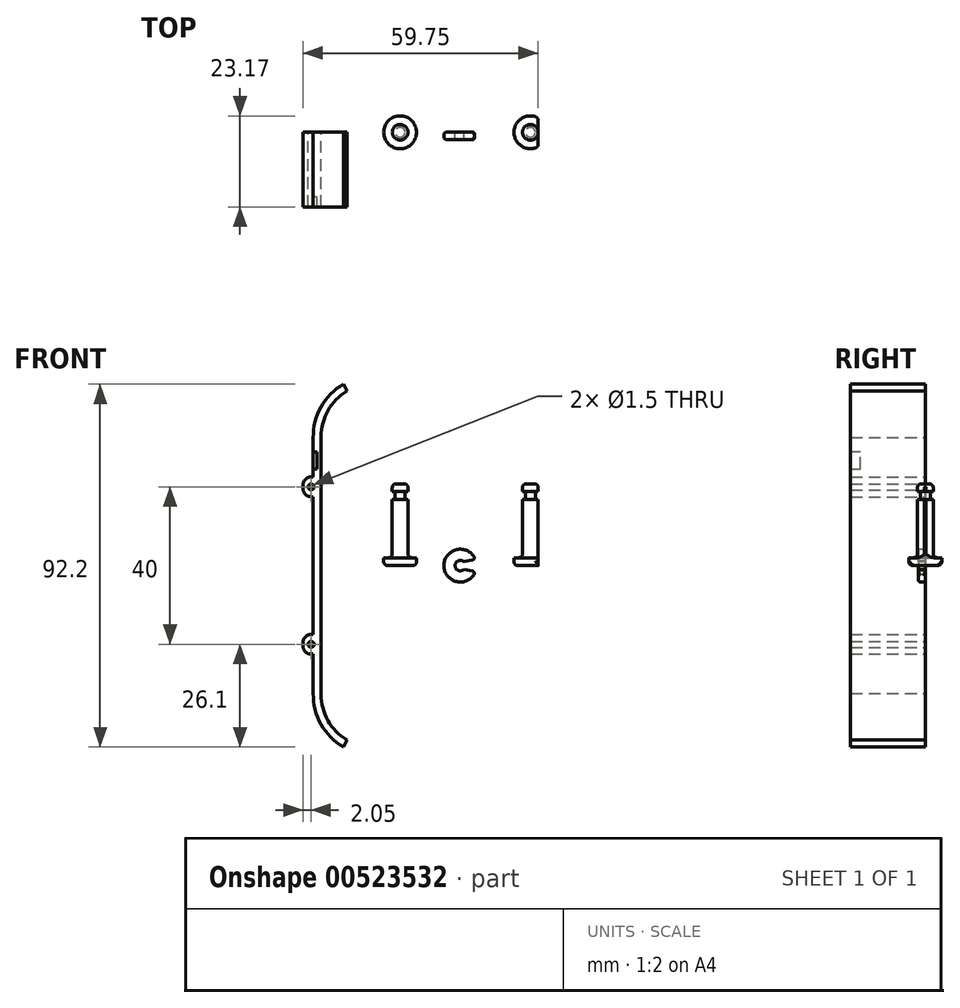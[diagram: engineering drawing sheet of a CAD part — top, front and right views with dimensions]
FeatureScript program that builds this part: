
annotation { "Feature Type Name" : "Feature", "Feature Type Description" : "" }
export const myFeature = defineFeature(function(context is Context, id is Id, definition is map)
    precondition{}
    {
        {
            var Q0;
            Q0=qCreatedBy(makeId("Front.planeOp"),FACE);
            var sketch = newSketch(context, id + "F0", { "sketchPlane" : qUnion([Q0])});
            skLineSegment(sketch, "E0", {"start": v(0, -32.75) * mm, "end": v(0, 32.75) * mm});
            skLineSegment(sketch, "E1", {"start": v(16.3, 46.1) * mm, "end": v(-10.09, 46.1) * mm, "construction": true});
            skLineSegment(sketch, "E2", {"start": v(9, 15.43) * mm, "end": v(9, 51.44) * mm, "construction": true});
            skArc(sketch, "E3.trimOffspring", {"start": v(6.55, 44.32) * mm, "mid": v(1.75, 39.4) * mm, "end": v(0, 32.75) * mm});
            skLineSegment(sketch, "E4", {"start": v(-2, -32.5) * mm, "end": v(-2, -22.5) * mm});
            skArc(sketch, "E5.trimOffspring", {"start": v(5.63, 46.1) * mm, "mid": v(-0.02, 40.33) * mm, "end": v(-2, 32.5) * mm});
            skLineSegment(sketch, "E6", {"start": v(-2, 17.5) * mm, "end": v(-4.6, 17.5) * mm});
            skLineSegment(sketch, "E7", {"start": v(-4.6, 17.5) * mm, "end": v(-4.6, 22.5) * mm});
            skLineSegment(sketch, "E8", {"start": v(-4.6, 22.5) * mm, "end": v(-2, 22.5) * mm});
            skCircle(sketch, "E9", {"center": v(-2.55, 20) * mm, "radius": 0.75 * mm});
            skLineSegment(sketch, "E10.trimOffspring", {"start": v(-2, 22.5) * mm, "end": v(-2, 32.5) * mm});
            skCircle(sketch, "E11.MirrorC", {"center": v(-2.55, -20) * mm, "radius": 0.75 * mm});
            skLineSegment(sketch, "E12.MirrorCS", {"start": v(-2, -17.5) * mm, "end": v(-4.6, -17.5) * mm});
            skLineSegment(sketch, "E13.MirrorCS", {"start": v(-4.6, -22.5) * mm, "end": v(-2, -22.5) * mm});
            skLineSegment(sketch, "E14.MirrorCS", {"start": v(-4.6, -17.5) * mm, "end": v(-4.6, -22.5) * mm});
            skLineSegment(sketch, "E15.trimOffspring", {"start": v(-2, -17.5) * mm, "end": v(-2, 17.5) * mm});
            skPoint(sketch, "E16", {"position": v(-0.02, 40.33) * mm});
            skPoint(sketch, "E17", {"position": v(1.75, 39.4) * mm});
            skLineSegment(sketch, "E18", {"start": v(5.63, 46.1) * mm, "end": v(6.55, 44.32) * mm});
            skArc(sketch, "E19.MirrorCS", {"start": v(6.55, -44.32) * mm, "mid": v(1.75, -39.4) * mm, "end": v(0, -32.75) * mm});
            skArc(sketch, "E20.MirrorCS", {"start": v(5.63, -46.1) * mm, "mid": v(-0.02, -40.33) * mm, "end": v(-2, -32.5) * mm});
            skLineSegment(sketch, "E21.MirrorCS", {"start": v(5.63, -46.1) * mm, "end": v(6.55, -44.32) * mm});
            skSolve(sketch);
        }
        {
            var Q0;
            Q0=makeQuery(id+"F0.imprint","IMPRINT",FACE,{"disambiguationData":[TD([[makeQuery(id+"F0.imprint","IMPRINT",EDGE,{"derivedFrom":sQuery(id+"F0.wireOp",EDGE,"E0")}),1.0]])]});
            extrude(context, id + "F1", {"entities" : qUnion([Q0]), "depth" : 19 * mm, "offsetDistance" : 25 * mm});
        }
        {
            var Q0;
            Q0=makeQuery(id+"F1.opExtrude","SWEPT_EDGE",EDGE,{"disambiguationData":[OSD([sQuery(id+"F0.wireOp",EDGE,"E7"),sQuery(id+"F0.wireOp",EDGE,"E8")])]});
            var Q1;
            Q1=makeQuery(id+"F1.opExtrude","SWEPT_EDGE",EDGE,{"disambiguationData":[OSD([sQuery(id+"F0.wireOp",EDGE,"E6"),sQuery(id+"F0.wireOp",EDGE,"E7")])]});
            var Q2;
            Q2=makeQuery(id+"F1.opExtrude","SWEPT_EDGE",EDGE,{"disambiguationData":[OSD([sQuery(id+"F0.wireOp",EDGE,"E12.MirrorCS"),sQuery(id+"F0.wireOp",EDGE,"E14.MirrorCS")])]});
            var Q3;
            Q3=makeQuery(id+"F1.opExtrude","SWEPT_EDGE",EDGE,{"disambiguationData":[OSD([sQuery(id+"F0.wireOp",EDGE,"E13.MirrorCS"),sQuery(id+"F0.wireOp",EDGE,"E14.MirrorCS")])]});
            fillet(context, id + "F2", {"entities" : qUnion([Q0, Q1, Q2, Q3]), "radius" : 2 * mm, "tangentPropagation" : true, "allowEdgeOverflow" : false});
        }
        {
            var Q0;
            Q0=makeQuery(id+"F1.opExtrude","SWEPT_FACE",FACE,{"disambiguationData":[OSD([sQuery(id+"F0.wireOp",EDGE,"E10.trimOffspring")])]});
            var sketch = newSketch(context, id + "F3", { "sketchPlane" : qUnion([Q0])});
            skLineSegment(sketch, "E22", {"start": v(19, 24.6) * mm, "end": v(16.5, 24.6) * mm});
            skLineSegment(sketch, "E23", {"start": v(16.5, 24.6) * mm, "end": v(16.5, 28.86) * mm});
            skLineSegment(sketch, "E24", {"start": v(16.5, 28.86) * mm, "end": v(19, 28.86) * mm});
            skLineSegment(sketch, "E25", {"start": v(19, 24.6) * mm, "end": v(19, 28.86) * mm});
            skSolve(sketch);
        }
        {
            var Q0;
            Q0=makeQuery(id+"F3.imprint","IMPRINT",FACE,{"disambiguationData":[TD([[makeQuery(id+"F3.imprint","IMPRINT",EDGE,{"derivedFrom":sQuery(id+"F3.wireOp",EDGE,"E22")}),-1.0]])]});
            extrude(context, id + "F4", {"entities" : qUnion([Q0]), "operationType" : NewBodyOperationType.REMOVE, "oppositeDirection" : true, "depth" : 1 * mm, "offsetDistance" : 25 * mm});
        }
        {
            var Q0;
            Q0=qCreatedBy(makeId("Front.planeOp"),FACE);
            var sketch = newSketch(context, id + "F5", { "sketchPlane" : qUnion([Q0])});
            skLineSegment(sketch, "E26", {"start": v(20.07, 0) * mm, "end": v(20.07, 24.62) * mm, "construction": true});
            skLineSegment(sketch, "E27", {"start": v(20.07, 0) * mm, "end": v(15.9, 0) * mm});
            skLineSegment(sketch, "E28", {"start": v(15.9, 0) * mm, "end": v(15.9, 2) * mm});
            skLineSegment(sketch, "E29", {"start": v(15.9, 2) * mm, "end": v(18.07, 2) * mm});
            skLineSegment(sketch, "E30", {"start": v(18.07, 2) * mm, "end": v(18.07, 16.8) * mm});
            skLineSegment(sketch, "E31", {"start": v(18.07, 16.8) * mm, "end": v(18.82, 16.8) * mm});
            skLineSegment(sketch, "E32", {"start": v(18.82, 16.8) * mm, "end": v(18.82, 18.8) * mm});
            skLineSegment(sketch, "E33", {"start": v(18.82, 18.8) * mm, "end": v(18.07, 18.8) * mm});
            skLineSegment(sketch, "E34", {"start": v(18.07, 18.8) * mm, "end": v(18.07, 20.8) * mm});
            skLineSegment(sketch, "E35", {"start": v(18.07, 20.8) * mm, "end": v(20.07, 20.8) * mm});
            skLineSegment(sketch, "E36", {"start": v(20.07, 20.8) * mm, "end": v(20.07, 0) * mm});
            skSolve(sketch);
        }
        {
            var Q0;
            Q0=makeQuery(id+"F5.imprint","IMPRINT",FACE,{"disambiguationData":[TD([[makeQuery(id+"F5.imprint","IMPRINT",EDGE,{"derivedFrom":sQuery(id+"F5.wireOp",EDGE,"E27")}),-1.0]])]});
            var Q1;
            Q1=sQuery(id+"F5.wireOp",EDGE,"E36");
            revolve(context, id + "F6", {"entities" : qUnion([Q0]), "axis" : qUnion([Q1]), "revolveType" : RevolveType.FULL});
        }
        {
            var Q0;
            Q0=makeQuery(id+"F6.opRevolve","SWEPT_EDGE",EDGE,{"disambiguationData":[OSD([sQuery(id+"F5.wireOp",EDGE,"E34"),sQuery(id+"F5.wireOp",EDGE,"E35")])]});
            var Q1;
            Q1=makeQuery(id+"F6.opRevolve","SWEPT_EDGE",EDGE,{"disambiguationData":[OSD([sQuery(id+"F5.wireOp",EDGE,"E27"),sQuery(id+"F5.wireOp",EDGE,"E28")])]});
            var Q2;
            Q2=makeQuery(id+"F6.opRevolve","SWEPT_EDGE",EDGE,{"disambiguationData":[OSD([sQuery(id+"F5.wireOp",EDGE,"E29"),sQuery(id+"F5.wireOp",EDGE,"E30")])]});
            fillet(context, id + "F7", {"entities" : qUnion([Q0, Q1, Q2]), "radius" : 1 * mm, "tangentPropagation" : true, "allowEdgeOverflow" : false});
        }
        {
            var Q0;
            Q0=qCreatedBy(makeId("Front.planeOp"),FACE);
            var sketch = newSketch(context, id + "F8", { "sketchPlane" : qUnion([Q0])});
            skArc(sketch, "E37", {"start": v(39.23, 1.56) * mm, "mid": v(31.2, 0) * mm, "end": v(39.23, -1.56) * mm});
            skArc(sketch, "E38", {"start": v(36.24, 1) * mm, "mid": v(34.04, 0) * mm, "end": v(36.24, -1) * mm});
            skLineSegment(sketch, "E39", {"start": v(36.24, 1) * mm, "end": v(39.23, 1.56) * mm});
            skLineSegment(sketch, "E40", {"start": v(36.24, -1) * mm, "end": v(39.23, -1.56) * mm});
            skSolve(sketch);
        }
        {
            var Q0;
            Q0=makeQuery(id+"F8.imprint","IMPRINT",FACE,{"disambiguationData":[TD([[makeQuery(id+"F8.imprint","IMPRINT",EDGE,{"derivedFrom":sQuery(id+"F8.wireOp",EDGE,"E37")}),1.0]])]});
            extrude(context, id + "F9", {"entities" : qUnion([Q0]), "depth" : 1.8 * mm, "offsetDistance" : 25 * mm});
        }
        {
            var Q0;
            Q0=makeQuery(id+"F9.opExtrude","CAP_EDGE",EDGE,{"disambiguationData":[OSD([sQuery(id+"F8.wireOp",EDGE,"E37")])],"isStart":false});
            var Q1;
            Q1=makeQuery(id+"F9.opExtrude","CAP_EDGE",EDGE,{"disambiguationData":[OSD([sQuery(id+"F8.wireOp",EDGE,"E37")])],"isStart":true});
            var Q2;
            Q2=makeQuery(id+"F9.opExtrude","SWEPT_EDGE",EDGE,{"disambiguationData":[OSD([sQuery(id+"F8.wireOp",EDGE,"E37"),sQuery(id+"F8.wireOp",EDGE,"E39")])]});
            var Q3;
            Q3=makeQuery(id+"F9.opExtrude","SWEPT_EDGE",EDGE,{"disambiguationData":[OSD([sQuery(id+"F8.wireOp",EDGE,"E37"),sQuery(id+"F8.wireOp",EDGE,"E40")])]});
            fillet(context, id + "F10", {"entities" : qUnion([Q0, Q1, Q2, Q3]), "radius" : .6 * mm, "tangentPropagation" : true, "allowEdgeOverflow" : false});
        }
        {
            var Q0;
            Q0=qCreatedBy(makeId("Front.planeOp"),FACE);
            var sketch = newSketch(context, id + "F11", { "sketchPlane" : qUnion([Q0])});
            skLineSegment(sketch, "E41", {"start": v(53.16, 0) * mm, "end": v(49, 0) * mm});
            skLineSegment(sketch, "E42", {"start": v(49, 0) * mm, "end": v(49, 2) * mm});
            skLineSegment(sketch, "E43", {"start": v(49, 2) * mm, "end": v(51.16, 2) * mm});
            skLineSegment(sketch, "E44", {"start": v(51.16, 2) * mm, "end": v(51.16, 16.8) * mm});
            skLineSegment(sketch, "E45", {"start": v(51.16, 16.8) * mm, "end": v(51.91, 16.8) * mm});
            skLineSegment(sketch, "E46", {"start": v(51.91, 16.8) * mm, "end": v(51.91, 18.8) * mm});
            skLineSegment(sketch, "E47", {"start": v(51.91, 18.8) * mm, "end": v(51.16, 18.8) * mm});
            skLineSegment(sketch, "E48", {"start": v(51.16, 18.8) * mm, "end": v(51.16, 20.8) * mm});
            skLineSegment(sketch, "E49", {"start": v(51.16, 20.8) * mm, "end": v(53.16, 20.8) * mm});
            skLineSegment(sketch, "E50", {"start": v(53.16, 20.8) * mm, "end": v(53.16, 0) * mm});
            skSolve(sketch);
        }
        {
            var Q0;
            Q0=makeQuery(id+"F11.imprint","IMPRINT",FACE,{"disambiguationData":[TD([[makeQuery(id+"F11.imprint","IMPRINT",EDGE,{"derivedFrom":sQuery(id+"F11.wireOp",EDGE,"E41")}),-1.0]])]});
            var Q1;
            Q1=sQuery(id+"F11.wireOp",EDGE,"E50");
            revolve(context, id + "F12", {"entities" : qUnion([Q0]), "axis" : qUnion([Q1]), "revolveType" : RevolveType.FULL});
        }
        {
            var Q0;
            Q0=qCreatedBy(makeId("Top.planeOp"),FACE);
            var sketch = newSketch(context, id + "F13", { "sketchPlane" : qUnion([Q0])});
            skLineSegment(sketch, "E51", {"start": v(55.15, -5) * mm, "end": v(55.15, 5) * mm});
            skLineSegment(sketch, "E52", {"start": v(55.15, 5) * mm, "end": v(57.86, 5) * mm});
            skLineSegment(sketch, "E53", {"start": v(57.86, 5) * mm, "end": v(57.86, -5) * mm});
            skLineSegment(sketch, "E54", {"start": v(57.86, -5) * mm, "end": v(55.15, -5) * mm});
            skSolve(sketch);
        }
        {
            var Q0;
            Q0 = qSketchRegion(id + "F13", true);
            extrude(context, id + "F14", {"entities" : qUnion([Q0]), "operationType" : NewBodyOperationType.REMOVE, "endBound" : BoundingType.SYMMETRIC, "oppositeDirection" : true, "depth" : 50 * mm, "offsetDistance" : 25 * mm});
        }
        {
            var Q0;
            Q0=makeQuery(id+"F12.opRevolve","SWEPT_EDGE",EDGE,{"disambiguationData":[OSD([sQuery(id+"F11.wireOp",EDGE,"E48"),sQuery(id+"F11.wireOp",EDGE,"E49")])]});
            var Q1;
            Q1=makeQuery(id+"F12.opRevolve","SWEPT_EDGE",EDGE,{"disambiguationData":[OSD([sQuery(id+"F11.wireOp",EDGE,"E41"),sQuery(id+"F11.wireOp",EDGE,"E42")])]});
            var Q2;
            Q2=makeQuery(id+"F12.opRevolve","SWEPT_EDGE",EDGE,{"disambiguationData":[OSD([sQuery(id+"F11.wireOp",EDGE,"E43"),sQuery(id+"F11.wireOp",EDGE,"E44")])]});
            var Q3;
            Q3=makeQuery(id+"F14.boolean.opBoolean","INTERSECT",EDGE,{"disambiguationData":[OD(0.0)],"derivedFrom":[makeQuery(id+"F12.opRevolve","SWEPT_FACE",FACE,{"disambiguationData":[OSD([sQuery(id+"F11.wireOp",EDGE,"E42")])]}),makeQuery(id+"F14.opExtrude","SWEPT_FACE",FACE,{"disambiguationData":[OSD([sQuery(id+"F13.wireOp",EDGE,"E51")])]})]});
            var Q4;
            Q4=makeQuery(id+"F14.boolean.opBoolean","INTERSECT",EDGE,{"disambiguationData":[OD(1.0)],"derivedFrom":[makeQuery(id+"F12.opRevolve","SWEPT_FACE",FACE,{"disambiguationData":[OSD([sQuery(id+"F11.wireOp",EDGE,"E42")])]}),makeQuery(id+"F14.opExtrude","SWEPT_FACE",FACE,{"disambiguationData":[OSD([sQuery(id+"F13.wireOp",EDGE,"E51")])]})]});
            fillet(context, id + "F15", {"entities" : qUnion([Q0, Q1, Q2, Q3, Q4]), "radius" : 1 * mm, "tangentPropagation" : true, "allowEdgeOverflow" : false});
        }
        {
            var Q0;
            Q0=makeQuery(id+"F4.boolean.opBoolean","COPY",FACE,{"derivedFrom":makeQuery(id+"F4.opExtrude","SWEPT_FACE",FACE,{"disambiguationData":[OSD([sQuery(id+"F3.wireOp",EDGE,"E23")])]})});
            var sketch = newSketch(context, id + "F16", { "sketchPlane" : qUnion([Q0])});
            skCircle(sketch, "E55", {"center": v(-3, 26.73) * mm, "radius": 2 * mm});
            skSolve(sketch);
        }
        {
            var Q0;
            {var subQ0=sQuery(id+"F16.wireOp",EDGE,"E55");var subQ1=sQuery(id+"F3.wireOp",EDGE,"E23");var subQ2=makeQuery(id+"F4.boolean.opBoolean","COPY",EDGE,{"derivedFrom":makeQuery(id+"F4.opExtrude","CAP_EDGE",EDGE,{"disambiguationData":[OSD([subQ1])],"isStart":true})});var subQ3=makeQuery(id+"F16.imprint","INTERSECT",VERTEX,{"disambiguationData":[OD(0.0)],"derivedFrom":[subQ2,subQ0]});Q0=makeQuery(id+"F16.imprint","IMPRINT",FACE,{"disambiguationData":[TD([[makeQuery(id+"F16.imprint","IMPRINT",EDGE,{"disambiguationData":[TD([[subQ3,1.0]])],"derivedFrom":subQ0}),1.0]])]});}
            extrude(context, id + "F17", {"entities" : qUnion([Q0]), "operationType" : NewBodyOperationType.REMOVE, "oppositeDirection" : true, "depth" : 5 * mm, "offsetDistance" : 25 * mm});
        }
    });
